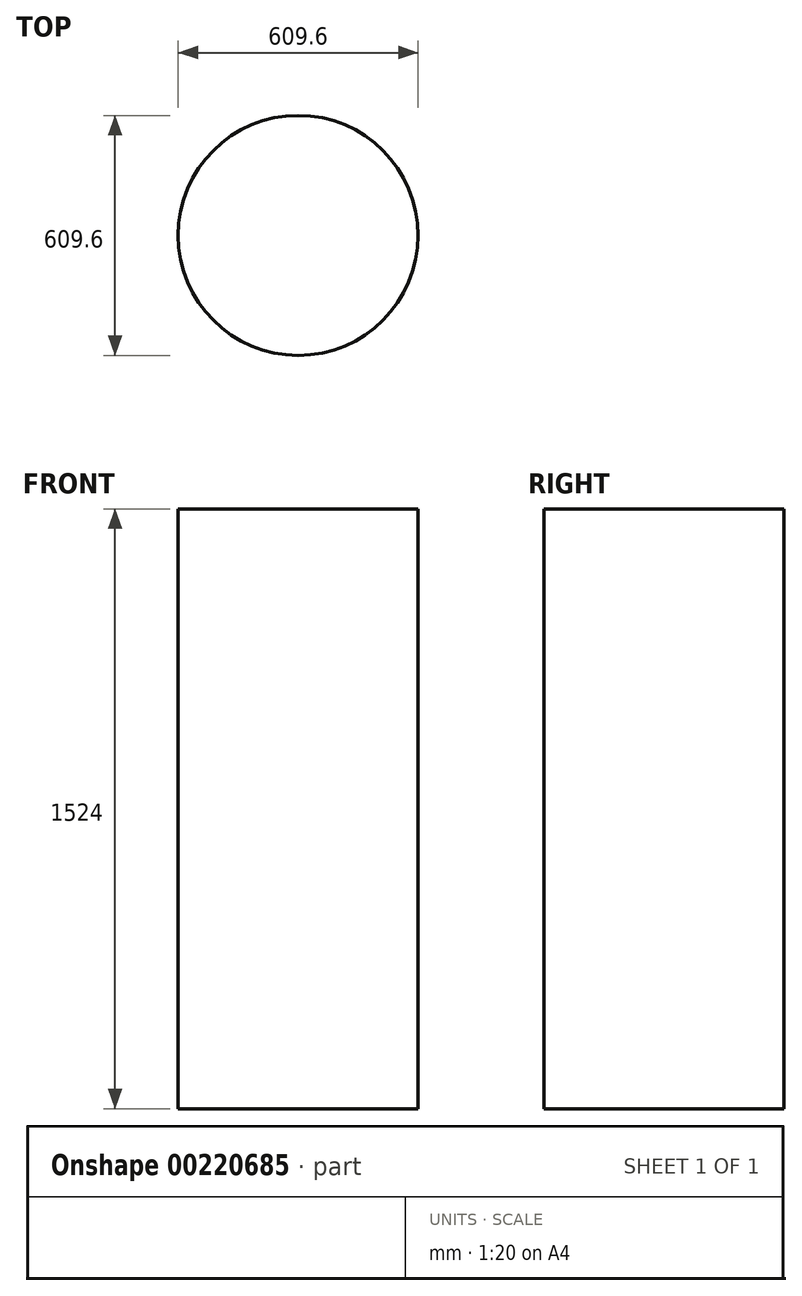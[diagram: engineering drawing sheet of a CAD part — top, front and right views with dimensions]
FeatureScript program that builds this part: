
annotation { "Feature Type Name" : "Feature", "Feature Type Description" : "" }
export const myFeature = defineFeature(function(context is Context, id is Id, definition is map)
    precondition{}
    {
        {
            var Q0;
            Q0=qCreatedBy(makeId("Top.planeOp"),FACE);
            var sketch = newSketch(context, id + "F0", { "sketchPlane" : qUnion([Q0])});
            skCircle(sketch, "E0", {"center": v(0, 0) * mm, "radius": 304.8 * mm});
            skSolve(sketch);
        }
        {
            var Q0;
            Q0 = qSketchRegion(id + "F0", true);
            extrude(context, id + "F1", {"entities" : qUnion([Q0]), "depth" : 1524 * mm});
        }
    });
